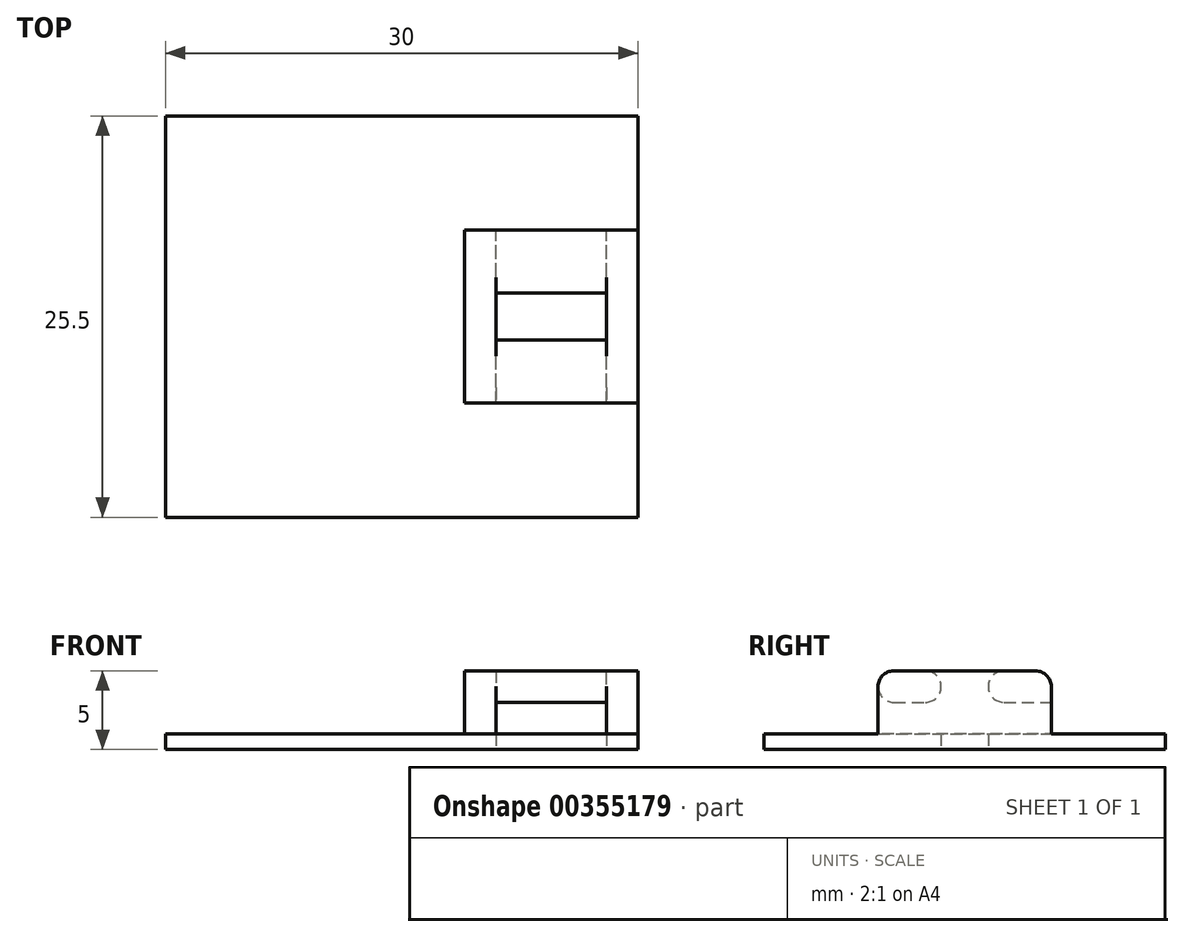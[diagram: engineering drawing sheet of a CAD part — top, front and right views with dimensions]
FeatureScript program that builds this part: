
annotation { "Feature Type Name" : "Feature", "Feature Type Description" : "" }
export const myFeature = defineFeature(function(context is Context, id is Id, definition is map)
    precondition{}
    {
        {
            var Q0;
            Q0=qCreatedBy(makeId("Top.planeOp"),FACE);
            var sketch = newSketch(context, id + "F0", { "sketchPlane" : qUnion([Q0])});
            skLineSegment(sketch, "E0.bottom", {"start": v(0, 0) * mm, "end": v(31, 0) * mm});
            skLineSegment(sketch, "E0.top", {"start": v(0, -27.5) * mm, "end": v(31, -27.5) * mm});
            skLineSegment(sketch, "E0.left", {"start": v(0, 0) * mm, "end": v(0, -27.5) * mm});
            skLineSegment(sketch, "E0.right", {"start": v(31, 0) * mm, "end": v(31, -27.5) * mm});
            skLineSegment(sketch, "E1.bottom", {"start": v(31, 0) * mm, "end": v(30, 0) * mm});
            skLineSegment(sketch, "E1.top", {"start": v(31, -27.5) * mm, "end": v(30, -27.5) * mm});
            skLineSegment(sketch, "E1.right", {"start": v(30, 0) * mm, "end": v(30, -27.5) * mm});
            skLineSegment(sketch, "E2.bottom", {"start": v(0, 0) * mm, "end": v(30, 0) * mm});
            skLineSegment(sketch, "E2.top", {"start": v(0, -1) * mm, "end": v(30, -1) * mm});
            skLineSegment(sketch, "E2.left", {"start": v(0, 0) * mm, "end": v(0, -1) * mm});
            skLineSegment(sketch, "E2.right", {"start": v(30, 0) * mm, "end": v(30, -1) * mm});
            skLineSegment(sketch, "E3.bottom", {"start": v(0, -27.5) * mm, "end": v(30, -27.5) * mm});
            skLineSegment(sketch, "E3.top", {"start": v(0, -26.5) * mm, "end": v(30, -26.5) * mm});
            skLineSegment(sketch, "E3.left", {"start": v(0, -27.5) * mm, "end": v(0, -26.5) * mm});
            skLineSegment(sketch, "E3.right", {"start": v(30, -27.5) * mm, "end": v(30, -26.5) * mm});
            skPoint(sketch, "E4", {"position": v(0, -13.75) * mm});
            skLineSegment(sketch, "E5", {"start": v(0, -13.75) * mm, "end": v(30, -13.75) * mm});
            skLineSegment(sketch, "E6.bottom", {"start": v(30, -13.75) * mm, "end": v(19, -13.75) * mm});
            skLineSegment(sketch, "E6.top", {"start": v(30, -19.25) * mm, "end": v(19, -19.25) * mm});
            skLineSegment(sketch, "E6.left", {"start": v(30, -13.75) * mm, "end": v(30, -19.25) * mm});
            skLineSegment(sketch, "E6.right", {"start": v(19, -13.75) * mm, "end": v(19, -19.25) * mm});
            skLineSegment(sketch, "E7.MirrorCS", {"start": v(19, -13.75) * mm, "end": v(19, -8.25) * mm});
            skLineSegment(sketch, "E8.MirrorCS", {"start": v(30, -8.25) * mm, "end": v(19, -8.25) * mm});
            skPoint(sketch, "E9", {"position": v(24.5, -13.75) * mm});
            skLineSegment(sketch, "E10.bottom", {"start": v(21, -15.25) * mm, "end": v(28, -15.25) * mm});
            skLineSegment(sketch, "E10.top", {"start": v(21, -12.25) * mm, "end": v(28, -12.25) * mm});
            skLineSegment(sketch, "E10.left", {"start": v(21, -15.25) * mm, "end": v(21, -12.25) * mm});
            skLineSegment(sketch, "E10.right", {"start": v(28, -15.25) * mm, "end": v(28, -12.25) * mm});
            skSolve(sketch);
        }
        {
            var Q0;
            Q0=makeQuery(id+"F0.imprint","IMPRINT",FACE,{"disambiguationData":[TD([[makeQuery(id+"F0.imprint","IMPRINT",EDGE,{"derivedFrom":sQuery(id+"F0.wireOp",EDGE,"E2.bottom")}),-1.0]])]});
            var Q1;
            Q1=makeQuery(id+"F0.imprint","IMPRINT",FACE,{"disambiguationData":[TD([[makeQuery(id+"F0.imprint","IMPRINT",EDGE,{"derivedFrom":sQuery(id+"F0.wireOp",EDGE,"E1.bottom")}),1.0]])]});
            var Q2;
            Q2=makeQuery(id+"F0.imprint","IMPRINT",FACE,{"disambiguationData":[TD([[makeQuery(id+"F0.imprint","IMPRINT",EDGE,{"derivedFrom":sQuery(id+"F0.wireOp",EDGE,"E3.bottom")}),1.0]])]});
            var Q3;
            {var subQ1=sQuery(id+"F0.wireOp",EDGE,"E2.top");Q3=makeQuery(id+"F0.imprint","IMPRINT",FACE,{"disambiguationData":[TD([[makeQuery(id+"F0.imprint","IMPRINT",EDGE,{"derivedFrom":subQ1}),-1.0]])]});}
            var Q4;
            {var subQ0=sQuery(id+"F0.wireOp",EDGE,"E3.top");Q4=makeQuery(id+"F0.imprint","IMPRINT",FACE,{"disambiguationData":[TD([[makeQuery(id+"F0.imprint","IMPRINT",EDGE,{"derivedFrom":subQ0}),1.0]])]});}
            extrude(context, id + "F1", {"entities" : qUnion([Q0, Q1, Q2, Q3, Q4]), "depth" : 5 * mm});
        }
        {
            var Q0;
            {var subQ0=sQuery(id+"F0.wireOp",EDGE,"E7.MirrorCS");Q0=makeQuery(id+"F0.imprint","IMPRINT",FACE,{"disambiguationData":[TD([[makeQuery(id+"F0.imprint","IMPRINT",EDGE,{"derivedFrom":subQ0}),-1.0]])]});}
            var Q1;
            Q1=makeQuery(id+"F0.imprint","IMPRINT",FACE,{"disambiguationData":[TD([[makeQuery(id+"F0.imprint","IMPRINT",EDGE,{"derivedFrom":sQuery(id+"F0.wireOp",EDGE,"E6.top")}),-1.0]])]});
            extrude(context, id + "F2", {"entities" : qUnion([Q0, Q1]), "operationType" : NewBodyOperationType.ADD, "depth" : 9 * mm});
        }
        {
            var Q0;
            {var subQ1=sQuery(id+"F0.wireOp",EDGE,"E2.top");Q0=makeQuery(id+"F0.imprint","IMPRINT",FACE,{"disambiguationData":[TD([[makeQuery(id+"F0.imprint","IMPRINT",EDGE,{"derivedFrom":subQ1}),-1.0]])]});}
            var Q1;
            {var subQ0=sQuery(id+"F0.wireOp",EDGE,"E3.top");Q1=makeQuery(id+"F0.imprint","IMPRINT",FACE,{"disambiguationData":[TD([[makeQuery(id+"F0.imprint","IMPRINT",EDGE,{"derivedFrom":subQ0}),1.0]])]});}
            var Q2;
            Q2=makeQuery(id+"F0.imprint","IMPRINT",FACE,{"disambiguationData":[TD([[makeQuery(id+"F0.imprint","IMPRINT",EDGE,{"derivedFrom":sQuery(id+"F0.wireOp",EDGE,"E6.top")}),-1.0]])]});
            var Q3;
            {var subQ0=sQuery(id+"F0.wireOp",EDGE,"E7.MirrorCS");Q3=makeQuery(id+"F0.imprint","IMPRINT",FACE,{"disambiguationData":[TD([[makeQuery(id+"F0.imprint","IMPRINT",EDGE,{"derivedFrom":subQ0}),-1.0]])]});}
            extrude(context, id + "F3", {"entities" : qUnion([Q0, Q1, Q2, Q3]), "operationType" : NewBodyOperationType.REMOVE, "depth" : 4 * mm});
        }
        {
            var Q0;
            Q0=makeQuery(id+"F2.opExtrude","SWEPT_FACE",FACE,{"disambiguationData":[OSD([sQuery(id+"F0.wireOp",EDGE,"E8.MirrorCS")])]});
            var sketch = newSketch(context, id + "F4", { "sketchPlane" : qUnion([Q0])});
            skPoint(sketch, "E11", {"position": v(-24.5, 5) * mm});
            skLineSegment(sketch, "E12.bottom", {"start": v(-24.5, 5) * mm, "end": v(-21, 5) * mm});
            skLineSegment(sketch, "E12.top", {"start": v(-24.5, 7) * mm, "end": v(-21, 7) * mm});
            skLineSegment(sketch, "E12.left", {"start": v(-24.5, 5) * mm, "end": v(-24.5, 7) * mm});
            skLineSegment(sketch, "E12.right", {"start": v(-21, 5) * mm, "end": v(-21, 7) * mm});
            skLineSegment(sketch, "E13.MirrorCS", {"start": v(-24.5, 7) * mm, "end": v(-28, 7) * mm});
            skLineSegment(sketch, "E14.MirrorCS", {"start": v(-28, 5) * mm, "end": v(-28, 7) * mm});
            skSolve(sketch);
        }
        {
            var Q0;
            {var subQ0=sQuery(id+"F4.wireOp",EDGE,"E12.left");Q0=makeQuery(id+"F4.imprint","IMPRINT",FACE,{"disambiguationData":[TD([[makeQuery(id+"F4.imprint","IMPRINT",EDGE,{"derivedFrom":subQ0}),1.0]])]});}
            var Q1;
            Q1=makeQuery(id+"F4.imprint","IMPRINT",FACE,{"disambiguationData":[TD([[makeQuery(id+"F4.imprint","IMPRINT",EDGE,{"derivedFrom":sQuery(id+"F4.wireOp",EDGE,"E12.bottom")}),1.0]])]});
            extrude(context, id + "F5", {"entities" : qUnion([Q0, Q1]), "operationType" : NewBodyOperationType.REMOVE, "oppositeDirection" : true, "depth" : 25 * mm});
        }
        {
            var Q0;
            Q0=makeQuery(id+"F2.opExtrude","CAP_EDGE",EDGE,{"disambiguationData":[OSD([sQuery(id+"F0.wireOp",EDGE,"E6.top")])],"isStart":false});
            var Q1;
            Q1=makeQuery(id+"F2.opExtrude","CAP_EDGE",EDGE,{"disambiguationData":[OSD([sQuery(id+"F0.wireOp",EDGE,"E10.top")])],"isStart":false});
            var Q2;
            Q2=makeQuery(id+"F5.boolean.opBoolean","INTERSECT",EDGE,{"derivedFrom":[makeQuery(id+"F2.opExtrude","SWEPT_FACE",FACE,{"disambiguationData":[OSD([sQuery(id+"F0.wireOp",EDGE,"E10.top")])]}),makeQuery(id+"F5.opExtrude","SWEPT_FACE",FACE,{"disambiguationData":[OSD([sQuery(id+"F4.wireOp",EDGE,"E12.top"),sQuery(id+"F4.wireOp",EDGE,"E13.MirrorCS")])]})]});
            var Q3;
            Q3=makeQuery(id+"F2.opExtrude","CAP_EDGE",EDGE,{"disambiguationData":[OSD([sQuery(id+"F0.wireOp",EDGE,"E8.MirrorCS")])],"isStart":false});
            var Q4;
            Q4=makeQuery(id+"F2.opExtrude","CAP_EDGE",EDGE,{"disambiguationData":[OSD([sQuery(id+"F0.wireOp",EDGE,"E10.bottom")])],"isStart":false});
            var Q5;
            Q5=makeQuery(id+"F5.boolean.opBoolean","INTERSECT",EDGE,{"derivedFrom":[makeQuery(id+"F2.opExtrude","SWEPT_FACE",FACE,{"disambiguationData":[OSD([sQuery(id+"F0.wireOp",EDGE,"E10.bottom")])]}),makeQuery(id+"F5.opExtrude","SWEPT_FACE",FACE,{"disambiguationData":[OSD([sQuery(id+"F4.wireOp",EDGE,"E12.top"),sQuery(id+"F4.wireOp",EDGE,"E13.MirrorCS")])]})]});
            var Q6;
            Q6=makeQuery(id+"F5.boolean.opBoolean","INTERSECT",EDGE,{"derivedFrom":[makeQuery(id+"F2.opExtrude","SWEPT_FACE",FACE,{"disambiguationData":[OSD([sQuery(id+"F0.wireOp",EDGE,"E6.top")])]}),makeQuery(id+"F5.opExtrude","SWEPT_FACE",FACE,{"disambiguationData":[OSD([sQuery(id+"F4.wireOp",EDGE,"E12.top"),sQuery(id+"F4.wireOp",EDGE,"E13.MirrorCS")])]})]});
            var Q7;
            Q7=makeQuery(id+"F5.boolean.opBoolean","COPY",EDGE,{"derivedFrom":makeQuery(id+"F5.opExtrude","CAP_EDGE",EDGE,{"disambiguationData":[OSD([sQuery(id+"F4.wireOp",EDGE,"E12.top"),sQuery(id+"F4.wireOp",EDGE,"E13.MirrorCS")])],"isStart":true})});
            fillet(context, id + "F6", {"entities" : qUnion([Q0, Q1, Q2, Q3, Q4, Q5, Q6, Q7]), "radius" : 1 * mm, "tangentPropagation" : true, "allowEdgeOverflow" : false});
        }
    });
